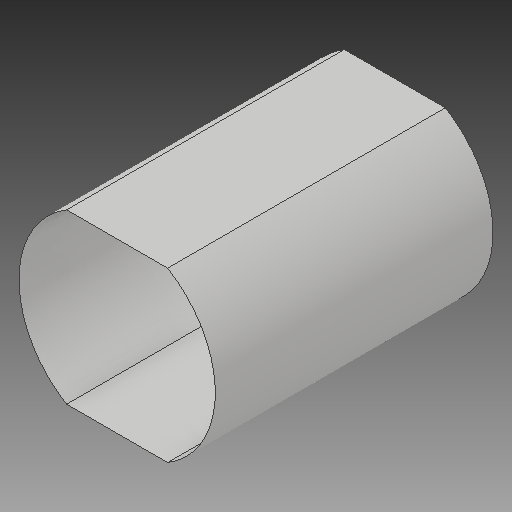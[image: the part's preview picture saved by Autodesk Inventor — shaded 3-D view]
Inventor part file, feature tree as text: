
AUTODESK INVENTOR PART (.ipt)
format: ipt  version: 2017 (Build 210142000, 142)  size: 111,616 bytes
history: native  units: in
note: dims shown in document units (in); Inventor stores cm internally (conversion verified against a paired STEP export)
features: extrude x1, delete_face x1, sketch x1
ambient origin geometry x8: Origin, YZ Plane, XZ Plane, XY Plane, X Axis, Y Axis, Z Axis, Center Point
bodies: Solid1 (feature_tree)
feature tree (3):
  extrude  "corridor"  Depth=3.8873in TaperAngle=0.0deg
  delete_face  "Delete Face1"
  sketch  "Sketch1"  dims[d0=6.6667in d1=4.0in d2=1.0in d3=11.0in d4=0.0in d7=1.0in d27=3.8873in d28=3.8873in d41=1.6458in d56=3.3333in]
